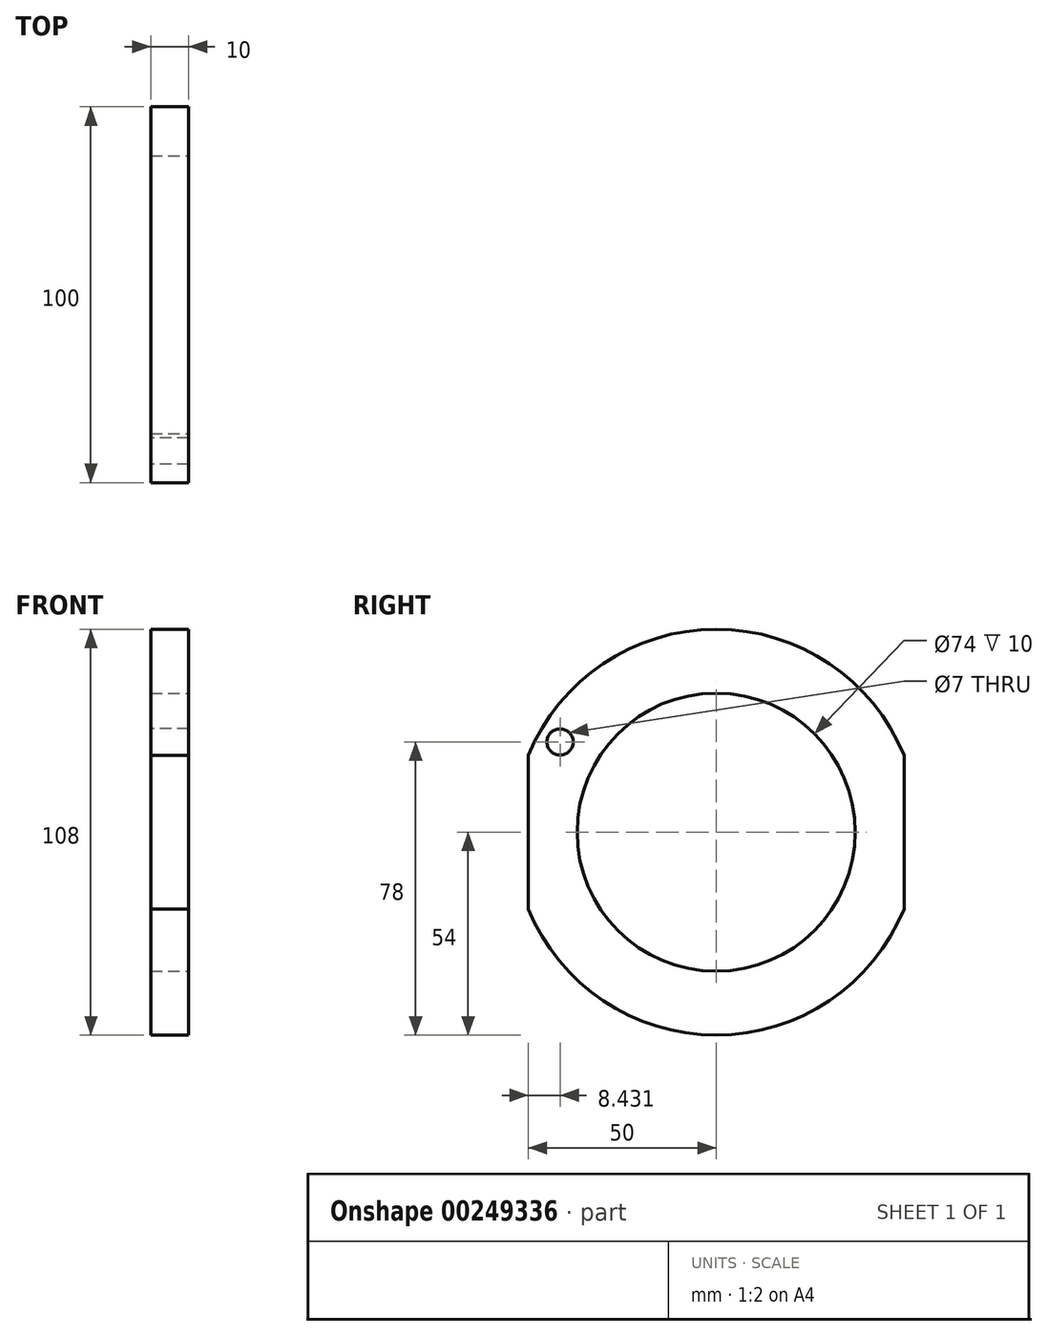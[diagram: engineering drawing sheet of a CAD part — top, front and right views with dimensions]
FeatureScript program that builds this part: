
annotation { "Feature Type Name" : "Feature", "Feature Type Description" : "" }
export const myFeature = defineFeature(function(context is Context, id is Id, definition is map)
    precondition{}
    {
        {
            var Q0;
            Q0=qCreatedBy(makeId("Front.planeOp"),FACE);
            var sketch = newSketch(context, id + "F0", { "sketchPlane" : qUnion([Q0])});
            skLineSegment(sketch, "E0", {"start": v(0, 0) * mm, "end": v(-57.54, 0) * mm, "construction": true});
            skLineSegment(sketch, "E1", {"start": v(0, 54) * mm, "end": v(0, 37) * mm});
            skLineSegment(sketch, "E2", {"start": v(0, 37) * mm, "end": v(10, 37) * mm});
            skLineSegment(sketch, "E3", {"start": v(10, 37) * mm, "end": v(10, 54) * mm});
            skLineSegment(sketch, "E4", {"start": v(0, 54) * mm, "end": v(10, 54) * mm});
            skSolve(sketch);
        }
        {
            var Q0;
            Q0=makeQuery(id+"F0.imprint","IMPRINT",FACE,{"disambiguationData":[TD([[makeQuery(id+"F0.imprint","IMPRINT",EDGE,{"derivedFrom":sQuery(id+"F0.wireOp",EDGE,"E1")}),1.0]])]});
            var Q1;
            Q1=sQuery(id+"F0.wireOp",EDGE,"E0");
            revolve(context, id + "F1", {"entities" : qUnion([Q0]), "axis" : qUnion([Q1]), "revolveType" : RevolveType.FULL});
        }
        {
            var Q0;
            Q0=makeQuery(id+"F1.opRevolve","SWEPT_FACE",FACE,{"disambiguationData":[OSD([sQuery(id+"F0.wireOp",EDGE,"E1")])]});
            var sketch = newSketch(context, id + "F2", { "sketchPlane" : qUnion([Q0])});
            skLineSegment(sketch, "E5", {"start": v(0, 0) * mm, "end": v(41.57, 24) * mm, "construction": true});
            skCircle(sketch, "E6", {"center": v(41.57, 24) * mm, "radius": 3.5 * mm});
            skSolve(sketch);
        }
        {
            var Q0;
            Q0=makeQuery(id+"F2.imprint","IMPRINT",FACE,{"disambiguationData":[TD([[makeQuery(id+"F2.imprint","IMPRINT",EDGE,{"derivedFrom":sQuery(id+"F2.wireOp",EDGE,"E6")}),1.0]])]});
            extrude(context, id + "F3", {"entities" : qUnion([Q0]), "operationType" : NewBodyOperationType.REMOVE, "endBound" : BoundingType.THROUGH_ALL, "oppositeDirection" : true, "depth" : 25 * mm, "offsetDistance" : 25 * mm});
        }
        {
            var Q0;
            Q0=makeQuery(id+"F1.opRevolve","SWEPT_FACE",FACE,{"disambiguationData":[OSD([sQuery(id+"F0.wireOp",EDGE,"E1")])]});
            var sketch = newSketch(context, id + "F4", { "sketchPlane" : qUnion([Q0])});
            skLineSegment(sketch, "E7", {"start": v(-50, 20.4) * mm, "end": v(-50, -20.4) * mm});
            skLineSegment(sketch, "E8", {"start": v(50, -20.4) * mm, "end": v(50, 20.4) * mm});
            skArc(sketch, "E9", {"start": v(50, -20.4) * mm, "mid": v(54, 0) * mm, "end": v(50, 20.4) * mm});
            skArc(sketch, "E10.trimOffspring", {"start": v(-50, 20.4) * mm, "mid": v(-54, 0) * mm, "end": v(-50, -20.4) * mm});
            skSolve(sketch);
        }
        {
            var Q0;
            Q0=makeQuery(id+"F4.imprint","IMPRINT",FACE,{"disambiguationData":[TD([[makeQuery(id+"F4.imprint","IMPRINT",EDGE,{"derivedFrom":sQuery(id+"F4.wireOp",EDGE,"E7")}),-1.0]])]});
            var Q1;
            Q1=makeQuery(id+"F4.imprint","IMPRINT",FACE,{"disambiguationData":[TD([[makeQuery(id+"F4.imprint","IMPRINT",EDGE,{"derivedFrom":sQuery(id+"F4.wireOp",EDGE,"E8")}),-1.0]])]});
            extrude(context, id + "F5", {"entities" : qUnion([Q0, Q1]), "operationType" : NewBodyOperationType.REMOVE, "endBound" : BoundingType.THROUGH_ALL, "oppositeDirection" : true, "depth" : 25 * mm, "offsetDistance" : 25 * mm});
        }
    });
